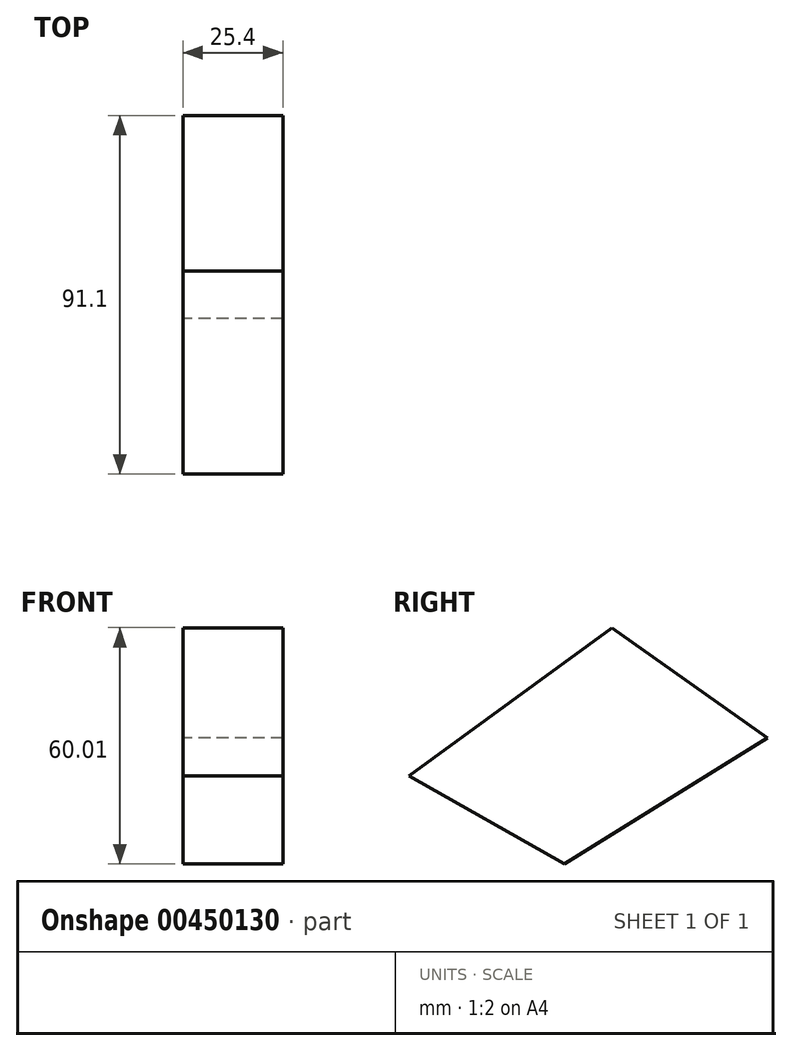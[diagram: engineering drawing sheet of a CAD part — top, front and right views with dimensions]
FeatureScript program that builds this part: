
annotation { "Feature Type Name" : "Feature", "Feature Type Description" : "" }
export const myFeature = defineFeature(function(context is Context, id is Id, definition is map)
    precondition{}
    {
        {
            var Q0;
            Q0=qCreatedBy(makeId("Right.planeOp"),FACE);
            var sketch = newSketch(context, id + "F0", { "sketchPlane" : qUnion([Q0])});
            skLineSegment(sketch, "E0", {"start": v(-32.38, 30.56) * mm, "end": v(0, 0) * mm});
            skLineSegment(sketch, "E1", {"start": v(0, 0) * mm, "end": v(62.01, 38.5) * mm});
            skLineSegment(sketch, "E2", {"start": v(62.01, 38.5) * mm, "end": v(22.5, 66.5) * mm});
            skLineSegment(sketch, "E3", {"start": v(22.5, 66.5) * mm, "end": v(-29.09, 28.86) * mm});
            skLineSegment(sketch, "E4", {"start": v(-29.09, 28.86) * mm, "end": v(82.9, -34.48) * mm});
            skLineSegment(sketch, "E5", {"start": v(82.9, -34.48) * mm, "end": v(49.29, -36.76) * mm});
            skLineSegment(sketch, "E6", {"start": v(49.29, -36.76) * mm, "end": v(-218.25, 140.26) * mm});
            skSolve(sketch);
        }
        {
            var Q0;
            {var subQ0=sQuery(id+"F0.wireOp",EDGE,"E2");Q0=makeQuery(id+"F0.imprint","IMPRINT",FACE,{"disambiguationData":[TD([[makeQuery(id+"F0.imprint","IMPRINT",EDGE,{"derivedFrom":subQ0}),1.0]])]});}
            extrude(context, id + "F1", {"entities" : qUnion([Q0]), "depth" : 25.4 * mm});
        }
    });
